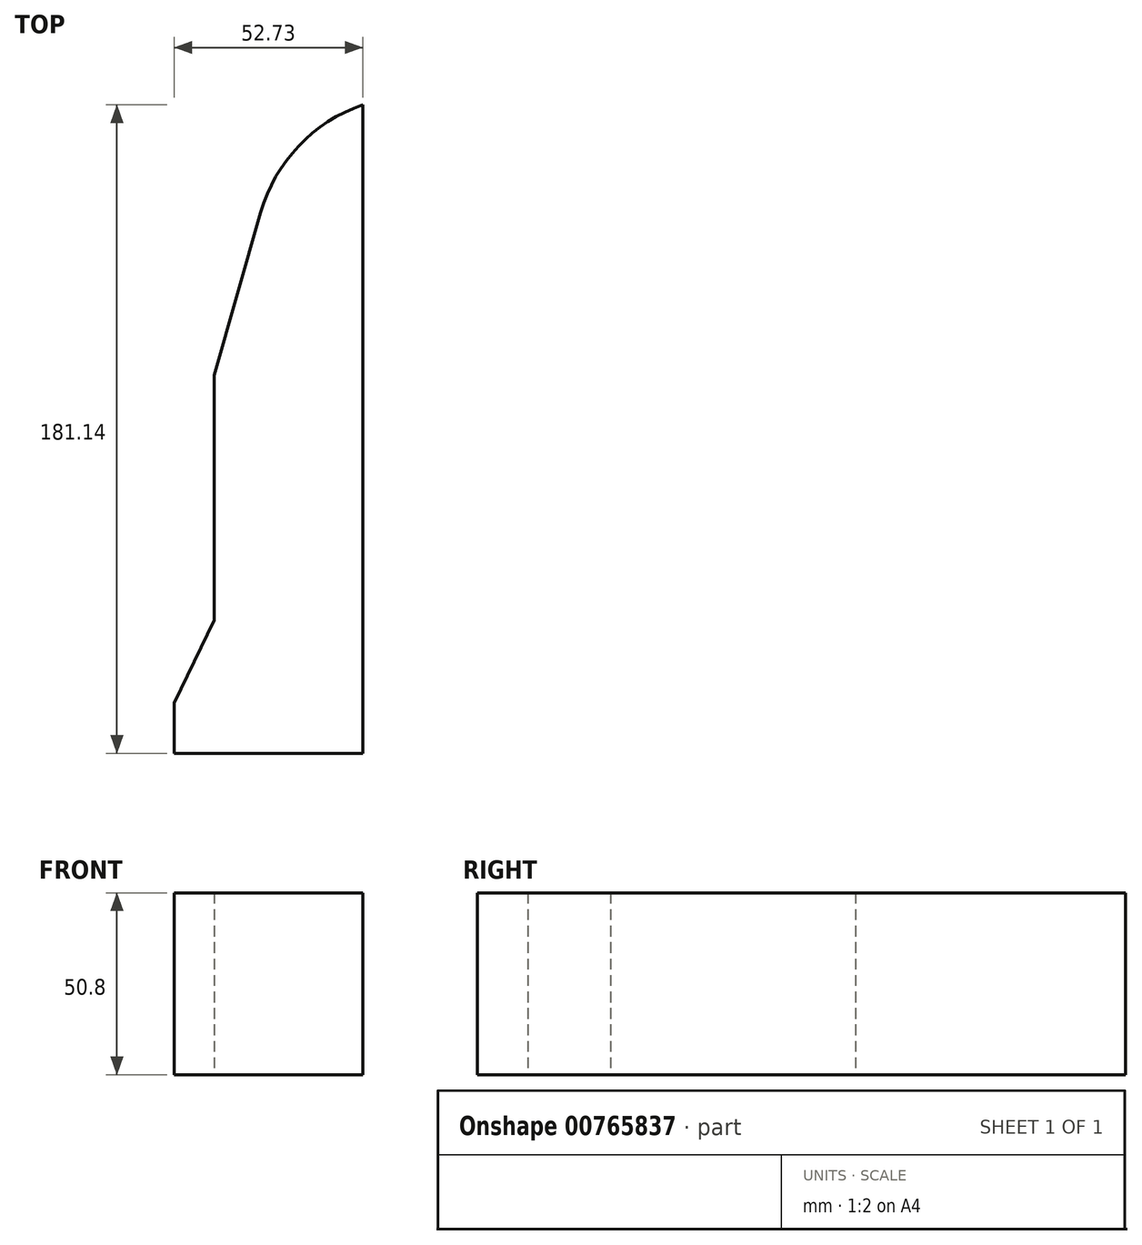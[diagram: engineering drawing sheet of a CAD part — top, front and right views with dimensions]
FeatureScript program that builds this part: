
annotation { "Feature Type Name" : "Feature", "Feature Type Description" : "" }
export const myFeature = defineFeature(function(context is Context, id is Id, definition is map)
    precondition{}
    {
        {
            var Q0;
            Q0=qCreatedBy(makeId("Top.planeOp"),FACE);
            var sketch = newSketch(context, id + "F0", { "sketchPlane" : qUnion([Q0])});
            skLineSegment(sketch, "E0", {"start": v(0, 0) * mm, "end": v(-52.73, 0) * mm});
            skLineSegment(sketch, "E1", {"start": v(-52.73, 0) * mm, "end": v(-52.73, 14.05) * mm});
            skLineSegment(sketch, "E2", {"start": v(-52.73, 14.05) * mm, "end": v(-41.5, 37.2) * mm});
            skLineSegment(sketch, "E3", {"start": v(-41.5, 37.2) * mm, "end": v(-41.5, 105.66) * mm});
            skLineSegment(sketch, "E4", {"start": v(-41.5, 105.66) * mm, "end": v(-28.52, 151.1) * mm});
            skArc(sketch, "E5", {"start": v(0, 181.14) * mm, "mid": v(-17.95, 169.62) * mm, "end": v(-28.52, 151.1) * mm});
            skLineSegment(sketch, "E6", {"start": v(0, 181.14) * mm, "end": v(0, 0) * mm});
            skSolve(sketch);
        }
        {
            var Q0;
            Q0=makeQuery(id+"F0.imprint","IMPRINT",FACE,{"disambiguationData":[TD([[makeQuery(id+"F0.imprint","IMPRINT",EDGE,{"derivedFrom":sQuery(id+"F0.wireOp",EDGE,"E0")}),-1.0]])]});
            extrude(context, id + "F1", {"entities" : qUnion([Q0]), "depth" : 50.8 * mm, "offsetDistance" : 25.4 * mm});
        }
    });
